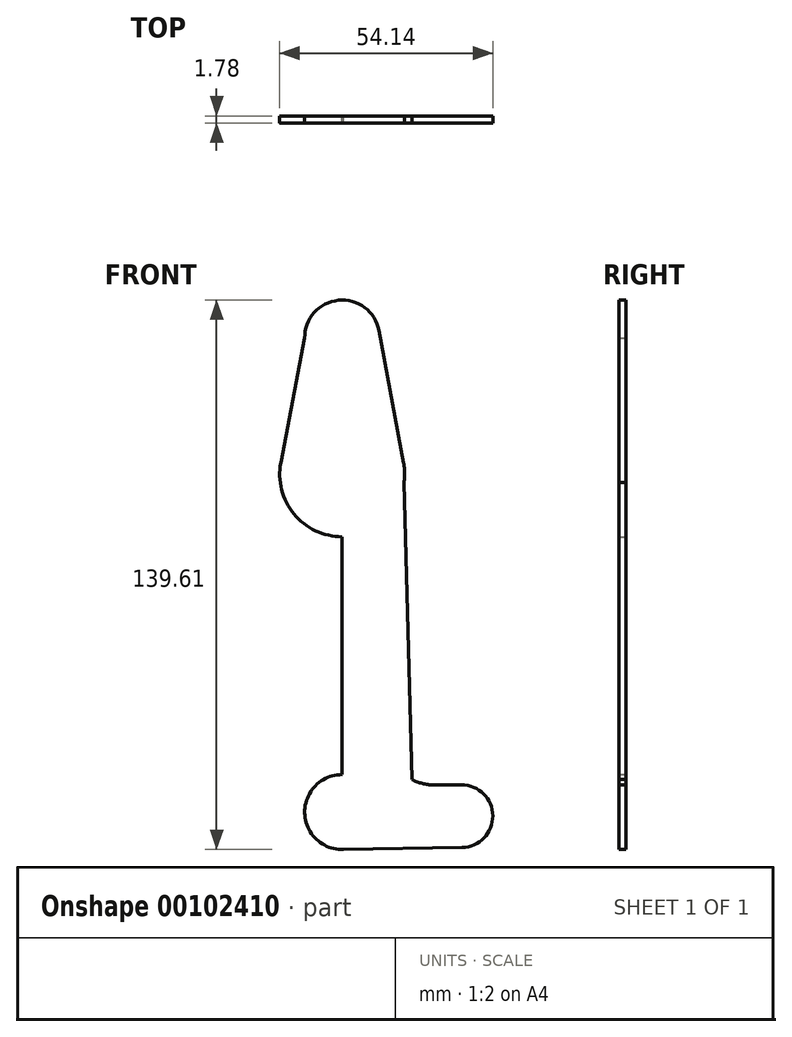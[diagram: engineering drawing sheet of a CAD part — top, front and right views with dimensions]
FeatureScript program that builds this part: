
annotation { "Feature Type Name" : "Feature", "Feature Type Description" : "" }
export const myFeature = defineFeature(function(context is Context, id is Id, definition is map)
    precondition{}
    {
        {
            var Q0;
            Q0=qCreatedBy(makeId("Front.planeOp"),FACE);
            var sketch = newSketch(context, id + "F0", { "sketchPlane" : qUnion([Q0])});
            skLineSegment(sketch, "E0", {"start": v(0, 120.57) * mm, "end": v(0, 0) * mm});
            skCircle(sketch, "E1", {"center": v(0, 120.57) * mm, "radius": 9.53 * mm});
            skCircle(sketch, "E2", {"center": v(0, 85.84) * mm, "radius": 15.88 * mm});
            skCircle(sketch, "E3", {"center": v(0, 0) * mm, "radius": 9.53 * mm});
            skCircle(sketch, "E4", {"center": v(30.33, -1.03) * mm, "radius": 7.94 * mm});
            skLineSegment(sketch, "E5", {"start": v(-9.52, 120.4) * mm, "end": v(-15.59, 88.83) * mm});
            skLineSegment(sketch, "E6", {"start": v(9.36, 122.3) * mm, "end": v(15.6, 88.74) * mm});
            skLineSegment(sketch, "E7", {"start": v(15.6, 88.74) * mm, "end": v(9.36, 122.3) * mm});
            skLineSegment(sketch, "E8", {"start": v(-15.59, 88.83) * mm, "end": v(-9.55, 0) * mm});
            skLineSegment(sketch, "E9", {"start": v(-9.55, 0) * mm, "end": v(-15.59, 88.83) * mm});
            skLineSegment(sketch, "E10", {"start": v(0, -9.53) * mm, "end": v(30.47, -8.97) * mm});
            skLineSegment(sketch, "E11", {"start": v(30.47, -8.97) * mm, "end": v(0, -9.52) * mm});
            skLineSegment(sketch, "E12", {"start": v(30.33, 6.9) * mm, "end": v(23.18, 6.9) * mm});
            skArc(sketch, "E13", {"start": v(17.7, 8.3) * mm, "mid": v(20.36, 7.26) * mm, "end": v(23.18, 6.9) * mm});
            skLineSegment(sketch, "E14", {"start": v(17.7, 8.3) * mm, "end": v(15.6, 88.74) * mm});
            skSolve(sketch);
        }
        {
            var Q0;
            Q0 = qSketchRegion(id + "F0", true);
            extrude(context, id + "F1", {"entities" : qUnion([Q0]), "depth" : 1.78 * mm});
        }
    });
